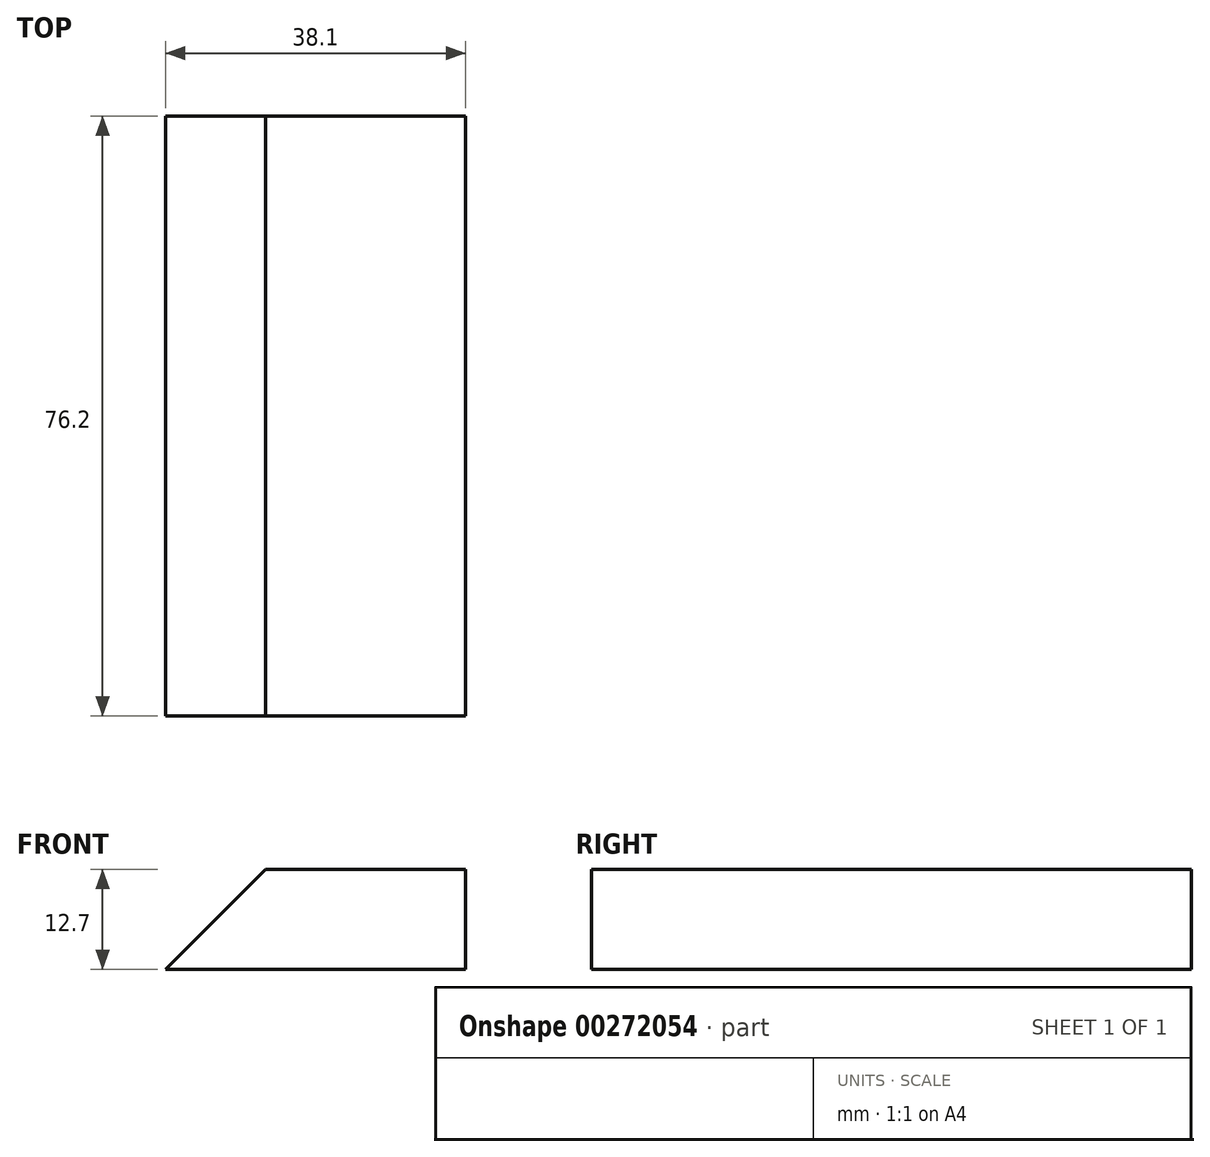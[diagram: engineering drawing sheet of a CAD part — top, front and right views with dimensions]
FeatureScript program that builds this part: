
annotation { "Feature Type Name" : "Feature", "Feature Type Description" : "" }
export const myFeature = defineFeature(function(context is Context, id is Id, definition is map)
    precondition{}
    {
        {
            var Q0;
            Q0=qCreatedBy(makeId("Top.planeOp"),FACE);
            var sketch = newSketch(context, id + "F0", { "sketchPlane" : qUnion([Q0])});
            skLineSegment(sketch, "E0.bottom", {"start": v(-14.63, 43.08) * mm, "end": v(23.47, 43.08) * mm});
            skLineSegment(sketch, "E0.top", {"start": v(-14.63, -33.12) * mm, "end": v(23.47, -33.12) * mm});
            skLineSegment(sketch, "E0.left", {"start": v(-14.63, 43.08) * mm, "end": v(-14.63, -33.12) * mm});
            skLineSegment(sketch, "E0.right", {"start": v(23.47, 43.08) * mm, "end": v(23.47, -33.12) * mm});
            skSolve(sketch);
        }
        {
            var Q0;
            Q0=makeQuery(id+"F0.imprint","IMPRINT",FACE,{"disambiguationData":[TD([[makeQuery(id+"F0.imprint","IMPRINT",EDGE,{"derivedFrom":sQuery(id+"F0.wireOp",EDGE,"E0.bottom")}),-1.0]])]});
            extrude(context, id + "F1", {"entities" : qUnion([Q0]), "depth" : 12.7 * mm});
        }
        {
            var Q0;
            Q0=makeQuery(id+"F1.opExtrude","CAP_EDGE",EDGE,{"disambiguationData":[OSD([sQuery(id+"F0.wireOp",EDGE,"E0.left")])],"isStart":false});
            chamfer(context, id + "F2", {"entities" : qUnion([Q0]), "chamferType" : ChamferType.TWO_OFFSETS, "width1" : 12.7 * mm, "oppositeDirection" : false, "width2" : 12.7 * mm, "tangentPropagation" : true});
        }
    });
